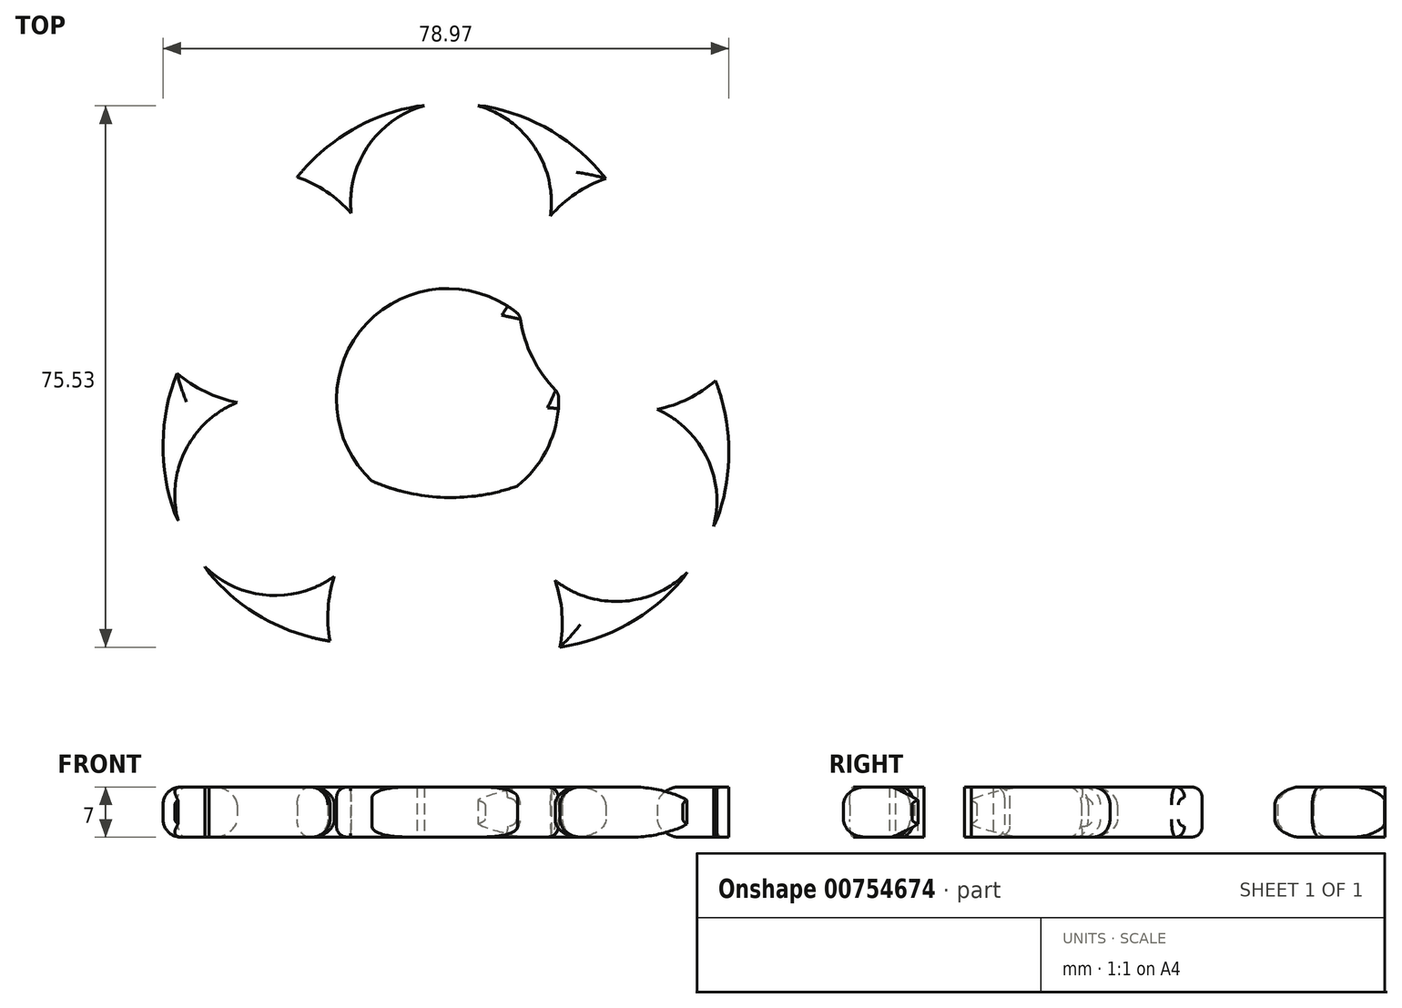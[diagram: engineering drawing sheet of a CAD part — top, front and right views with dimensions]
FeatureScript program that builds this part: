
annotation { "Feature Type Name" : "Feature", "Feature Type Description" : "" }
export const myFeature = defineFeature(function(context is Context, id is Id, definition is map)
    precondition{}
    {
        {
            var Q0;
            Q0=qCreatedBy(makeId("Top.planeOp"),FACE);
            var sketch = newSketch(context, id + "F0", { "sketchPlane" : qUnion([Q0])});
            skLineSegment(sketch, "E0.bottom", {"start": v(13.26, -12) * mm, "end": v(-14.74, -12) * mm});
            skLineSegment(sketch, "E0.top", {"start": v(13.74, 15.5) * mm, "end": v(-14.26, 15.5) * mm});
            skPoint(sketch, "E0.middle", {"position": v(-0.5, 1.75) * mm});
            skCircle(sketch, "E1", {"center": v(-0.26, 15.5) * mm, "radius": 14 * mm});
            skCircle(sketch, "E2", {"center": v(-0.26, 15.5) * mm, "radius": 11.05 * mm});
            skCircle(sketch, "E3", {"center": v(-0.74, -12) * mm, "radius": 15.5 * mm});
            skCircle(sketch, "E4", {"center": v(-0.74, -12) * mm, "radius": 11.05 * mm});
            skCircle(sketch, "E5", {"center": v(-0.28, 1.83) * mm, "radius": 27.5 * mm});
            skCircle(sketch, "E6", {"center": v(27.22, 1.83) * mm, "radius": 18 * mm});
            skCircle(sketch, "E7", {"center": v(-27.78, 1.83) * mm, "radius": 18.25 * mm});
            skCircle(sketch, "E8", {"center": v(-0.28, -33.4) * mm, "radius": 62.5 * mm});
            skSolve(sketch);
        }
        {
            var Q0;
            {var subQ0=sQuery(id+"F0.wireOp",EDGE,"E1");var subQ1=sQuery(id+"F0.wireOp",EDGE,"E0.top");var subQ2=makeQuery(id+"F0.imprint","INTERSECT",VERTEX,{"disambiguationData":[OD(0.0)],"derivedFrom":[subQ1,subQ0]});Q0=makeQuery(id+"F0.imprint","IMPRINT",FACE,{"disambiguationData":[TD([[makeQuery(id+"F0.imprint","IMPRINT",EDGE,{"disambiguationData":[TD([[subQ2,-1.0]])],"derivedFrom":subQ1}),-1.0]])]});}
            var Q1;
            {var subQ1=sQuery(id+"F0.wireOp",EDGE,"E1");var subQ7=makeQuery(id+"F0.imprint","INTERSECT",VERTEX,{"disambiguationData":[OD(0.0)],"derivedFrom":[sQuery(id+"F0.wireOp",EDGE,"E0.top"),subQ1]});Q1=makeQuery(id+"F0.imprint","IMPRINT",FACE,{"disambiguationData":[TD([[makeQuery(id+"F0.imprint","IMPRINT",EDGE,{"disambiguationData":[TD([[subQ7,-1.0]])],"derivedFrom":subQ1}),-1.0]])]});}
            var Q2;
            {var subQ1=sQuery(id+"F0.wireOp",EDGE,"E1");var subQ8=makeQuery(id+"F0.imprint","INTERSECT",VERTEX,{"disambiguationData":[OD(1.0)],"derivedFrom":[sQuery(id+"F0.wireOp",EDGE,"E0.top"),subQ1]});Q2=makeQuery(id+"F0.imprint","IMPRINT",FACE,{"disambiguationData":[TD([[makeQuery(id+"F0.imprint","IMPRINT",EDGE,{"disambiguationData":[TD([[subQ8,1.0]])],"derivedFrom":subQ1}),-1.0]])]});}
            var Q3;
            {var subQ0=sQuery(id+"F0.wireOp",EDGE,"E1");var subQ1=sQuery(id+"F0.wireOp",EDGE,"E0.top");var subQ10=makeQuery(id+"F0.imprint","INTERSECT",VERTEX,{"disambiguationData":[OD(0.0)],"derivedFrom":[subQ1,subQ0]});Q3=makeQuery(id+"F0.imprint","IMPRINT",FACE,{"disambiguationData":[TD([[makeQuery(id+"F0.imprint","IMPRINT",EDGE,{"disambiguationData":[TD([[subQ10,-1.0]])],"derivedFrom":subQ1}),1.0]])]});}
            var Q4;
            {var subQ0=sQuery(id+"F0.wireOp",EDGE,"E3");var subQ7=sQuery(id+"F0.wireOp",EDGE,"E0.bottom");var subQ13=makeQuery(id+"F0.imprint","INTERSECT",VERTEX,{"disambiguationData":[OD(0.0)],"derivedFrom":[subQ7,subQ0]});Q4=makeQuery(id+"F0.imprint","IMPRINT",FACE,{"disambiguationData":[TD([[makeQuery(id+"F0.imprint","IMPRINT",EDGE,{"disambiguationData":[TD([[subQ13,-1.0]])],"derivedFrom":subQ7}),-1.0]])]});}
            var Q5;
            {var subQ0=sQuery(id+"F0.wireOp",EDGE,"E3");var subQ1=sQuery(id+"F0.wireOp",EDGE,"E0.bottom");var subQ2=makeQuery(id+"F0.imprint","INTERSECT",VERTEX,{"disambiguationData":[OD(0.0)],"derivedFrom":[subQ1,subQ0]});Q5=makeQuery(id+"F0.imprint","IMPRINT",FACE,{"disambiguationData":[TD([[makeQuery(id+"F0.imprint","IMPRINT",EDGE,{"disambiguationData":[TD([[subQ2,-1.0]])],"derivedFrom":subQ1}),1.0]])]});}
            var Q6;
            {var subQ0=sQuery(id+"F0.wireOp",EDGE,"E7");var subQ1=sQuery(id+"F0.wireOp",EDGE,"E3");var subQ2=makeQuery(id+"F0.imprint","INTERSECT",VERTEX,{"disambiguationData":[OD(0.0)],"derivedFrom":[subQ1,subQ0]});Q6=makeQuery(id+"F0.imprint","IMPRINT",FACE,{"disambiguationData":[TD([[makeQuery(id+"F0.imprint","IMPRINT",EDGE,{"disambiguationData":[TD([[subQ2,-1.0]])],"derivedFrom":subQ1}),1.0]])]});}
            var Q7;
            {var subQ0=sQuery(id+"F0.wireOp",EDGE,"E6");var subQ1=sQuery(id+"F0.wireOp",EDGE,"E3");var subQ2=makeQuery(id+"F0.imprint","INTERSECT",VERTEX,{"disambiguationData":[OD(0.0)],"derivedFrom":[subQ1,subQ0]});Q7=makeQuery(id+"F0.imprint","IMPRINT",FACE,{"disambiguationData":[TD([[makeQuery(id+"F0.imprint","IMPRINT",EDGE,{"disambiguationData":[TD([[subQ2,-1.0]])],"derivedFrom":subQ1}),1.0]])]});}
            var Q8;
            {var subQ0=sQuery(id+"F0.wireOp",EDGE,"E3");var subQ1=sQuery(id+"F0.wireOp",EDGE,"E1");var subQ2=makeQuery(id+"F0.imprint","INTERSECT",VERTEX,{"disambiguationData":[OD(0.0)],"derivedFrom":[subQ1,subQ0]});Q8=makeQuery(id+"F0.imprint","IMPRINT",FACE,{"disambiguationData":[TD([[makeQuery(id+"F0.imprint","IMPRINT",EDGE,{"disambiguationData":[TD([[subQ2,-1.0]])],"derivedFrom":subQ1}),1.0]])]});}
            extrude(context, id + "F1", {"entities" : qUnion([Q0, Q1, Q2, Q3, Q4, Q5, Q6, Q7, Q8]), "depth" : 7 * mm, "offsetDistance" : 25 * mm});
        }
        {
            var Q0;
            {var subQ0=sQuery(id+"F0.wireOp",EDGE,"E5");Q0=makeQuery(id+"F1.opExtrude","CAP_EDGE",EDGE,{"disambiguationData":[OSD([subQ0]),TDD([makeQuery(id+"F0.imprint","IMPRINT",EDGE,{"disambiguationData":[TD([[makeQuery(id+"F0.imprint","INTERSECT",VERTEX,{"disambiguationData":[OD(0.0)],"derivedFrom":[subQ0,sQuery(id+"F0.wireOp",EDGE,"E8")]}),1.0]])],"derivedFrom":subQ0})])],"isStart":false});}
            var Q1;
            Q1=makeQuery(id+"F1.opExtrude","CAP_EDGE",EDGE,{"disambiguationData":[OSD([sQuery(id+"F0.wireOp",EDGE,"E6")])],"isStart":false});
            var Q2;
            Q2=makeQuery(id+"F1.opExtrude","CAP_EDGE",EDGE,{"disambiguationData":[OSD([sQuery(id+"F0.wireOp",EDGE,"E7")])],"isStart":false});
            var Q3;
            Q3=makeQuery(id+"F1.opExtrude","CAP_EDGE",EDGE,{"disambiguationData":[OSD([sQuery(id+"F0.wireOp",EDGE,"E6")])],"isStart":true});
            var Q4;
            {var subQ0=sQuery(id+"F0.wireOp",EDGE,"E5");Q4=makeQuery(id+"F1.opExtrude","CAP_EDGE",EDGE,{"disambiguationData":[OSD([subQ0]),TDD([makeQuery(id+"F0.imprint","IMPRINT",EDGE,{"disambiguationData":[TD([[makeQuery(id+"F0.imprint","INTERSECT",VERTEX,{"disambiguationData":[OD(0.0)],"derivedFrom":[subQ0,sQuery(id+"F0.wireOp",EDGE,"E8")]}),1.0]])],"derivedFrom":subQ0})])],"isStart":true});}
            var Q5;
            Q5=makeQuery(id+"F1.opExtrude","CAP_EDGE",EDGE,{"disambiguationData":[OSD([sQuery(id+"F0.wireOp",EDGE,"E7")])],"isStart":true});
            fillet(context, id + "F2", {"entities" : qUnion([Q0, Q1, Q2, Q3, Q4, Q5]), "radius" : 2.5 * mm, "tangentPropagation" : true, "allowEdgeOverflow" : false});
        }
        {
            var Q0;
            Q0=makeQuery(id+"F1.opExtrude","SWEPT_BODY",BODY,{"disambiguationData":[OSD([sQuery(id+"F0.wireOp",EDGE,"E1"),sQuery(id+"F0.wireOp",EDGE,"E2"),sQuery(id+"F0.wireOp",EDGE,"E3"),sQuery(id+"F0.wireOp",EDGE,"E4"),sQuery(id+"F0.wireOp",EDGE,"E5"),sQuery(id+"F0.wireOp",EDGE,"E6"),sQuery(id+"F0.wireOp",EDGE,"E7"),sQuery(id+"F0.wireOp",EDGE,"E8")])]});
            var Q1;
            {var subQ0=sQuery(id+"F0.wireOp",EDGE,"E3");var subQ1=makeQuery(id+"F0.imprint","INTERSECT",VERTEX,{"disambiguationData":[OD(0.0)],"derivedFrom":[sQuery(id+"F0.wireOp",EDGE,"E0.bottom"),subQ0]});var subQ2=sQuery(id+"F0.wireOp",EDGE,"E6");var subQ4=makeQuery(id+"F0.imprint","INTERSECT",VERTEX,{"disambiguationData":[OD(0.0)],"derivedFrom":[subQ0,subQ2]});Q1=makeQuery(id+"F1.opExtrude","SWEPT_FACE",FACE,{"disambiguationData":[OSD([subQ0]),TDD([makeQuery(id+"F0.imprint","IMPRINT",EDGE,{"disambiguationData":[TD([[subQ1,-1.0]])],"derivedFrom":subQ0}),makeQuery(id+"F0.imprint","IMPRINT",EDGE,{"disambiguationData":[TD([[subQ4,-1.0]])],"derivedFrom":subQ0}),makeQuery(id+"F0.imprint","IMPRINT",EDGE,{"disambiguationData":[TD([[makeQuery(id+"F0.imprint","INTERSECT",VERTEX,{"disambiguationData":[OD(1.0)],"derivedFrom":[sQuery(id+"F0.wireOp",EDGE,"E1"),subQ0]}),1.0]])],"derivedFrom":subQ0}),makeQuery(id+"F0.imprint","IMPRINT",EDGE,{"disambiguationData":[TD([[subQ1,1.0]])],"derivedFrom":subQ0})])]});}
            circularPattern(context, id + "F3", {"entities" : qUnion([Q0]), "axis" : qUnion([Q1]), "angle" : 360 * degree, "instanceCount" : 3, "equalSpace" : true});
        }
        {
            var Q0;
            Q0=makeQuery(id+"F1.opExtrude","SWEPT_BODY",BODY,{"disambiguationData":[OSD([sQuery(id+"F0.wireOp",EDGE,"E1"),sQuery(id+"F0.wireOp",EDGE,"E2"),sQuery(id+"F0.wireOp",EDGE,"E3"),sQuery(id+"F0.wireOp",EDGE,"E4"),sQuery(id+"F0.wireOp",EDGE,"E5"),sQuery(id+"F0.wireOp",EDGE,"E6"),sQuery(id+"F0.wireOp",EDGE,"E7"),sQuery(id+"F0.wireOp",EDGE,"E8")])]});
            var Q1;
            Q1=makeQuery(id+"F3.opPattern","COPY",BODY,{"derivedFrom":makeQuery(id+"F1.opExtrude","SWEPT_BODY",BODY,{"disambiguationData":[OSD([sQuery(id+"F0.wireOp",EDGE,"E1"),sQuery(id+"F0.wireOp",EDGE,"E2"),sQuery(id+"F0.wireOp",EDGE,"E3"),sQuery(id+"F0.wireOp",EDGE,"E4"),sQuery(id+"F0.wireOp",EDGE,"E5"),sQuery(id+"F0.wireOp",EDGE,"E6"),sQuery(id+"F0.wireOp",EDGE,"E7"),sQuery(id+"F0.wireOp",EDGE,"E8")])]}),"instanceName":"1"});
            var Q2;
            Q2=makeQuery(id+"F3.opPattern","COPY",BODY,{"derivedFrom":makeQuery(id+"F1.opExtrude","SWEPT_BODY",BODY,{"disambiguationData":[OSD([sQuery(id+"F0.wireOp",EDGE,"E1"),sQuery(id+"F0.wireOp",EDGE,"E2"),sQuery(id+"F0.wireOp",EDGE,"E3"),sQuery(id+"F0.wireOp",EDGE,"E4"),sQuery(id+"F0.wireOp",EDGE,"E5"),sQuery(id+"F0.wireOp",EDGE,"E6"),sQuery(id+"F0.wireOp",EDGE,"E7"),sQuery(id+"F0.wireOp",EDGE,"E8")])]}),"instanceName":"2"});
            var Q3;
            Q3=makeQuery(id+"F3.opPattern","COPY",BODY,{"derivedFrom":makeQuery(id+"F1.opExtrude","SWEPT_BODY",BODY,{"disambiguationData":[OSD([sQuery(id+"F0.wireOp",EDGE,"E1"),sQuery(id+"F0.wireOp",EDGE,"E2"),sQuery(id+"F0.wireOp",EDGE,"E3"),sQuery(id+"F0.wireOp",EDGE,"E4"),sQuery(id+"F0.wireOp",EDGE,"E5"),sQuery(id+"F0.wireOp",EDGE,"E6"),sQuery(id+"F0.wireOp",EDGE,"E7"),sQuery(id+"F0.wireOp",EDGE,"E8")])]}),"instanceName":"3"});
            booleanBodies(context, id + "F4", {"operationType" : BooleanOperationType.UNION, "tools" : qUnion([Q0, Q1, Q2, Q3])});
        }
        {
            var Q0;
            {var subQ0=sQuery(id+"F0.wireOp",EDGE,"E6");var subQ1=sQuery(id+"F0.wireOp",EDGE,"E3");var subQ3=makeQuery(id+"F1.opExtrude","CAP_EDGE",EDGE,{"disambiguationData":[OSD([subQ1]),TDD([makeQuery(id+"F0.imprint","IMPRINT",EDGE,{"disambiguationData":[TD([[makeQuery(id+"F0.imprint","INTERSECT",VERTEX,{"disambiguationData":[OD(1.0)],"derivedFrom":[subQ1,subQ0]}),1.0]])],"derivedFrom":subQ1})])],"isStart":false});var subQ4=sQuery(id+"F0.wireOp",EDGE,"E7");var subQ5=makeQuery(id+"F0.imprint","INTERSECT",VERTEX,{"disambiguationData":[OD(1.0)],"derivedFrom":[subQ1,subQ4]});var subQ6=makeQuery(id+"F0.imprint","INTERSECT",VERTEX,{"disambiguationData":[OD(0.0)],"derivedFrom":[subQ1,subQ4]});var subQ7=sQuery(id+"F0.wireOp",EDGE,"E1");Q0=makeQuery(id+"F4.opBoolean","MERGE",EDGE,{"derivedFrom":[makeQuery(id+"F1.opExtrude","CAP_EDGE",EDGE,{"disambiguationData":[OSD([subQ1]),TDD([makeQuery(id+"F0.imprint","IMPRINT",EDGE,{"disambiguationData":[TD([[makeQuery(id+"F0.imprint","INTERSECT",VERTEX,{"disambiguationData":[OD(1.0)],"derivedFrom":[subQ7,subQ1]}),1.0]])],"derivedFrom":subQ1})])],"isStart":false}),subQ3,makeQuery(id+"F3.opPattern","COPY",EDGE,{"derivedFrom":makeQuery(id+"F1.opExtrude","CAP_EDGE",EDGE,{"disambiguationData":[OSD([subQ1]),TDD([makeQuery(id+"F0.imprint","IMPRINT",EDGE,{"disambiguationData":[TD([[makeQuery(id+"F0.imprint","INTERSECT",VERTEX,{"disambiguationData":[OD(0.0)],"derivedFrom":[subQ7,subQ1]}),-1.0]])],"derivedFrom":subQ1}),makeQuery(id+"F0.imprint","IMPRINT",EDGE,{"disambiguationData":[TD([[subQ6,-1.0]])],"derivedFrom":subQ1}),makeQuery(id+"F0.imprint","IMPRINT",EDGE,{"disambiguationData":[TD([[subQ5,-1.0]])],"derivedFrom":subQ1})])],"isStart":false}),"instanceName":"1"}),makeQuery(id+"F3.opPattern","COPY",EDGE,{"derivedFrom":subQ3,"instanceName":"2"})]});}
            var Q1;
            {var subQ0=sQuery(id+"F0.wireOp",EDGE,"E7");var subQ1=sQuery(id+"F0.wireOp",EDGE,"E3");var subQ2=makeQuery(id+"F0.imprint","INTERSECT",VERTEX,{"disambiguationData":[OD(1.0)],"derivedFrom":[subQ1,subQ0]});var subQ3=makeQuery(id+"F0.imprint","INTERSECT",VERTEX,{"disambiguationData":[OD(0.0)],"derivedFrom":[subQ1,subQ0]});Q1=makeQuery(id+"F1.opExtrude","CAP_EDGE",EDGE,{"disambiguationData":[OSD([subQ1]),TDD([makeQuery(id+"F0.imprint","IMPRINT",EDGE,{"disambiguationData":[TD([[makeQuery(id+"F0.imprint","INTERSECT",VERTEX,{"disambiguationData":[OD(0.0)],"derivedFrom":[sQuery(id+"F0.wireOp",EDGE,"E1"),subQ1]}),-1.0]])],"derivedFrom":subQ1}),makeQuery(id+"F0.imprint","IMPRINT",EDGE,{"disambiguationData":[TD([[subQ3,-1.0]])],"derivedFrom":subQ1}),makeQuery(id+"F0.imprint","IMPRINT",EDGE,{"disambiguationData":[TD([[subQ2,-1.0]])],"derivedFrom":subQ1})])],"isStart":false});}
            var Q2;
            {var subQ0=sQuery(id+"F0.wireOp",EDGE,"E7");var subQ1=sQuery(id+"F0.wireOp",EDGE,"E3");var subQ2=makeQuery(id+"F0.imprint","INTERSECT",VERTEX,{"disambiguationData":[OD(1.0)],"derivedFrom":[subQ1,subQ0]});var subQ4=makeQuery(id+"F0.imprint","INTERSECT",VERTEX,{"disambiguationData":[OD(0.0)],"derivedFrom":[subQ1,subQ0]});var subQ5=sQuery(id+"F0.wireOp",EDGE,"E1");var subQ6=sQuery(id+"F0.wireOp",EDGE,"E6");Q2=makeQuery(id+"F4.opBoolean","MERGE",EDGE,{"derivedFrom":[makeQuery(id+"F3.opPattern","COPY",EDGE,{"derivedFrom":makeQuery(id+"F1.opExtrude","CAP_EDGE",EDGE,{"disambiguationData":[OSD([subQ1]),TDD([makeQuery(id+"F0.imprint","IMPRINT",EDGE,{"disambiguationData":[TD([[makeQuery(id+"F0.imprint","INTERSECT",VERTEX,{"disambiguationData":[OD(1.0)],"derivedFrom":[subQ5,subQ1]}),1.0]])],"derivedFrom":subQ1})])],"isStart":false}),"instanceName":"1"}),makeQuery(id+"F3.opPattern","COPY",EDGE,{"derivedFrom":makeQuery(id+"F1.opExtrude","CAP_EDGE",EDGE,{"disambiguationData":[OSD([subQ1]),TDD([makeQuery(id+"F0.imprint","IMPRINT",EDGE,{"disambiguationData":[TD([[makeQuery(id+"F0.imprint","INTERSECT",VERTEX,{"disambiguationData":[OD(1.0)],"derivedFrom":[subQ1,subQ6]}),1.0]])],"derivedFrom":subQ1})])],"isStart":false}),"instanceName":"1"}),makeQuery(id+"F3.opPattern","COPY",EDGE,{"derivedFrom":makeQuery(id+"F1.opExtrude","CAP_EDGE",EDGE,{"disambiguationData":[OSD([subQ1]),TDD([makeQuery(id+"F0.imprint","IMPRINT",EDGE,{"disambiguationData":[TD([[makeQuery(id+"F0.imprint","INTERSECT",VERTEX,{"disambiguationData":[OD(0.0)],"derivedFrom":[subQ5,subQ1]}),-1.0]])],"derivedFrom":subQ1}),makeQuery(id+"F0.imprint","IMPRINT",EDGE,{"disambiguationData":[TD([[subQ4,-1.0]])],"derivedFrom":subQ1}),makeQuery(id+"F0.imprint","IMPRINT",EDGE,{"disambiguationData":[TD([[subQ2,-1.0]])],"derivedFrom":subQ1})])],"isStart":false}),"instanceName":"2"})]});}
            var Q3;
            {var subQ0=sQuery(id+"F0.wireOp",EDGE,"E6");var subQ1=sQuery(id+"F0.wireOp",EDGE,"E3");var subQ3=makeQuery(id+"F1.opExtrude","CAP_EDGE",EDGE,{"disambiguationData":[OSD([subQ1]),TDD([makeQuery(id+"F0.imprint","IMPRINT",EDGE,{"disambiguationData":[TD([[makeQuery(id+"F0.imprint","INTERSECT",VERTEX,{"disambiguationData":[OD(1.0)],"derivedFrom":[subQ1,subQ0]}),1.0]])],"derivedFrom":subQ1})])],"isStart":true});var subQ4=sQuery(id+"F0.wireOp",EDGE,"E7");var subQ5=makeQuery(id+"F0.imprint","INTERSECT",VERTEX,{"disambiguationData":[OD(1.0)],"derivedFrom":[subQ1,subQ4]});var subQ6=makeQuery(id+"F0.imprint","INTERSECT",VERTEX,{"disambiguationData":[OD(0.0)],"derivedFrom":[subQ1,subQ4]});var subQ7=sQuery(id+"F0.wireOp",EDGE,"E1");Q3=makeQuery(id+"F4.opBoolean","MERGE",EDGE,{"derivedFrom":[makeQuery(id+"F1.opExtrude","CAP_EDGE",EDGE,{"disambiguationData":[OSD([subQ1]),TDD([makeQuery(id+"F0.imprint","IMPRINT",EDGE,{"disambiguationData":[TD([[makeQuery(id+"F0.imprint","INTERSECT",VERTEX,{"disambiguationData":[OD(1.0)],"derivedFrom":[subQ7,subQ1]}),1.0]])],"derivedFrom":subQ1})])],"isStart":true}),subQ3,makeQuery(id+"F3.opPattern","COPY",EDGE,{"derivedFrom":makeQuery(id+"F1.opExtrude","CAP_EDGE",EDGE,{"disambiguationData":[OSD([subQ1]),TDD([makeQuery(id+"F0.imprint","IMPRINT",EDGE,{"disambiguationData":[TD([[makeQuery(id+"F0.imprint","INTERSECT",VERTEX,{"disambiguationData":[OD(0.0)],"derivedFrom":[subQ7,subQ1]}),-1.0]])],"derivedFrom":subQ1}),makeQuery(id+"F0.imprint","IMPRINT",EDGE,{"disambiguationData":[TD([[subQ6,-1.0]])],"derivedFrom":subQ1}),makeQuery(id+"F0.imprint","IMPRINT",EDGE,{"disambiguationData":[TD([[subQ5,-1.0]])],"derivedFrom":subQ1})])],"isStart":true}),"instanceName":"1"}),makeQuery(id+"F3.opPattern","COPY",EDGE,{"derivedFrom":subQ3,"instanceName":"2"})]});}
            var Q4;
            {var subQ0=sQuery(id+"F0.wireOp",EDGE,"E7");var subQ1=sQuery(id+"F0.wireOp",EDGE,"E3");var subQ2=makeQuery(id+"F0.imprint","INTERSECT",VERTEX,{"disambiguationData":[OD(1.0)],"derivedFrom":[subQ1,subQ0]});var subQ3=makeQuery(id+"F0.imprint","INTERSECT",VERTEX,{"disambiguationData":[OD(0.0)],"derivedFrom":[subQ1,subQ0]});Q4=makeQuery(id+"F1.opExtrude","CAP_EDGE",EDGE,{"disambiguationData":[OSD([subQ1]),TDD([makeQuery(id+"F0.imprint","IMPRINT",EDGE,{"disambiguationData":[TD([[makeQuery(id+"F0.imprint","INTERSECT",VERTEX,{"disambiguationData":[OD(0.0)],"derivedFrom":[sQuery(id+"F0.wireOp",EDGE,"E1"),subQ1]}),-1.0]])],"derivedFrom":subQ1}),makeQuery(id+"F0.imprint","IMPRINT",EDGE,{"disambiguationData":[TD([[subQ3,-1.0]])],"derivedFrom":subQ1}),makeQuery(id+"F0.imprint","IMPRINT",EDGE,{"disambiguationData":[TD([[subQ2,-1.0]])],"derivedFrom":subQ1})])],"isStart":true});}
            var Q5;
            {var subQ0=sQuery(id+"F0.wireOp",EDGE,"E7");var subQ1=sQuery(id+"F0.wireOp",EDGE,"E3");var subQ2=makeQuery(id+"F0.imprint","INTERSECT",VERTEX,{"disambiguationData":[OD(1.0)],"derivedFrom":[subQ1,subQ0]});var subQ4=makeQuery(id+"F0.imprint","INTERSECT",VERTEX,{"disambiguationData":[OD(0.0)],"derivedFrom":[subQ1,subQ0]});var subQ5=sQuery(id+"F0.wireOp",EDGE,"E1");var subQ6=sQuery(id+"F0.wireOp",EDGE,"E6");Q5=makeQuery(id+"F4.opBoolean","MERGE",EDGE,{"derivedFrom":[makeQuery(id+"F3.opPattern","COPY",EDGE,{"derivedFrom":makeQuery(id+"F1.opExtrude","CAP_EDGE",EDGE,{"disambiguationData":[OSD([subQ1]),TDD([makeQuery(id+"F0.imprint","IMPRINT",EDGE,{"disambiguationData":[TD([[makeQuery(id+"F0.imprint","INTERSECT",VERTEX,{"disambiguationData":[OD(1.0)],"derivedFrom":[subQ5,subQ1]}),1.0]])],"derivedFrom":subQ1})])],"isStart":true}),"instanceName":"1"}),makeQuery(id+"F3.opPattern","COPY",EDGE,{"derivedFrom":makeQuery(id+"F1.opExtrude","CAP_EDGE",EDGE,{"disambiguationData":[OSD([subQ1]),TDD([makeQuery(id+"F0.imprint","IMPRINT",EDGE,{"disambiguationData":[TD([[makeQuery(id+"F0.imprint","INTERSECT",VERTEX,{"disambiguationData":[OD(1.0)],"derivedFrom":[subQ1,subQ6]}),1.0]])],"derivedFrom":subQ1})])],"isStart":true}),"instanceName":"1"}),makeQuery(id+"F3.opPattern","COPY",EDGE,{"derivedFrom":makeQuery(id+"F1.opExtrude","CAP_EDGE",EDGE,{"disambiguationData":[OSD([subQ1]),TDD([makeQuery(id+"F0.imprint","IMPRINT",EDGE,{"disambiguationData":[TD([[makeQuery(id+"F0.imprint","INTERSECT",VERTEX,{"disambiguationData":[OD(0.0)],"derivedFrom":[subQ5,subQ1]}),-1.0]])],"derivedFrom":subQ1}),makeQuery(id+"F0.imprint","IMPRINT",EDGE,{"disambiguationData":[TD([[subQ4,-1.0]])],"derivedFrom":subQ1}),makeQuery(id+"F0.imprint","IMPRINT",EDGE,{"disambiguationData":[TD([[subQ2,-1.0]])],"derivedFrom":subQ1})])],"isStart":true}),"instanceName":"2"})]});}
            fillet(context, id + "F5", {"entities" : qUnion([Q0, Q1, Q2, Q3, Q4, Q5]), "radius" : 1.5 * mm, "tangentPropagation" : true, "allowEdgeOverflow" : false});
        }
    });
